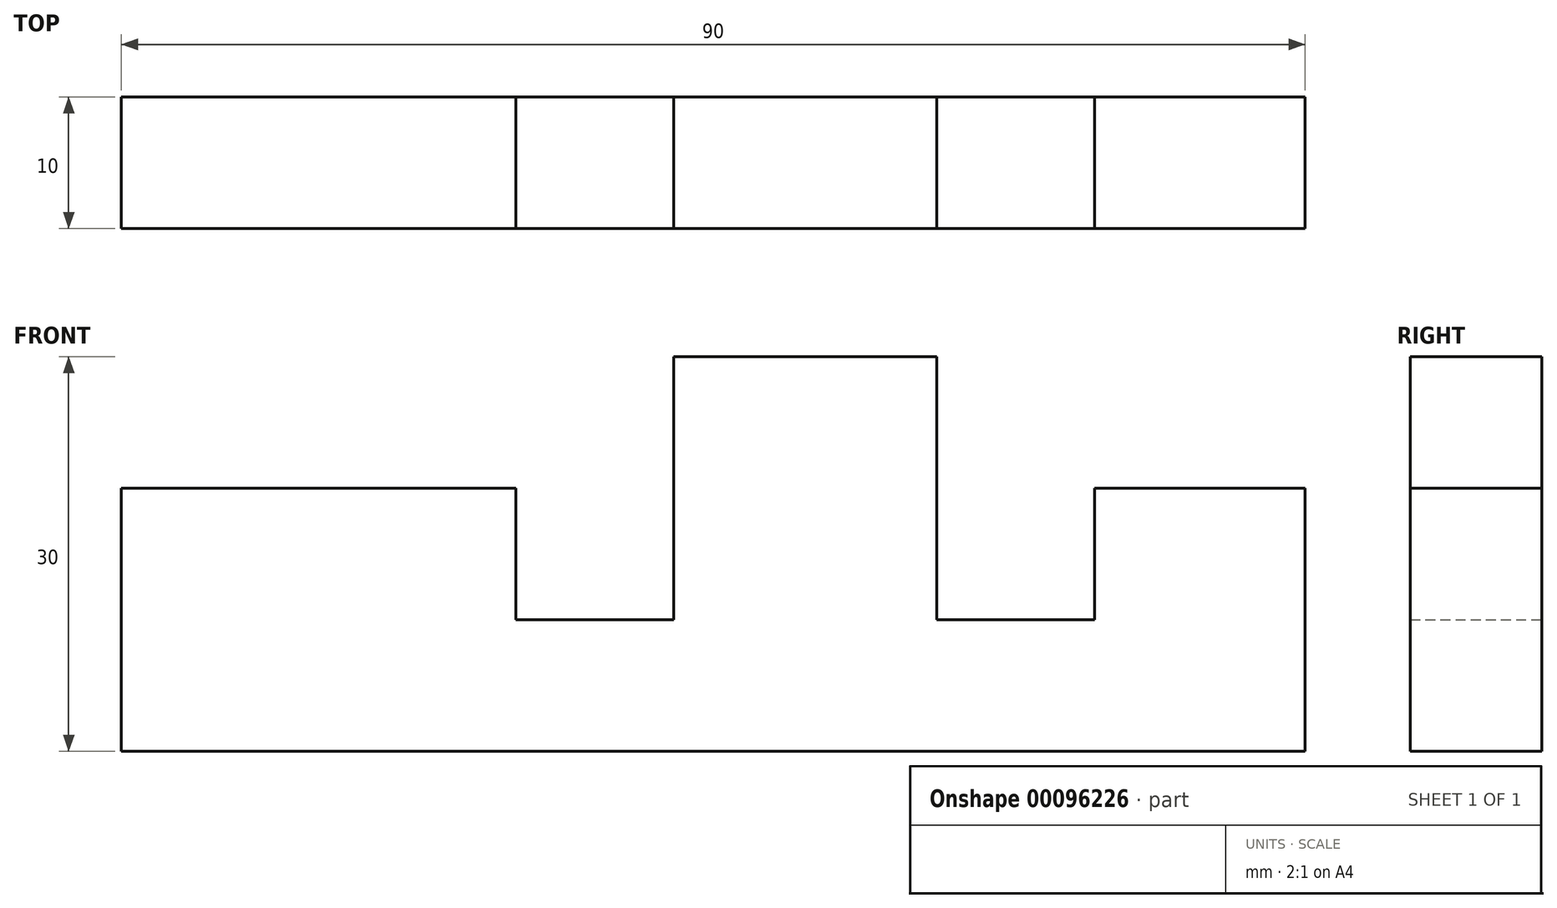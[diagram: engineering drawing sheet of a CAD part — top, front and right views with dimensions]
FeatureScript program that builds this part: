
annotation { "Feature Type Name" : "Feature", "Feature Type Description" : "" }
export const myFeature = defineFeature(function(context is Context, id is Id, definition is map)
    precondition{}
    {
        {
            var Q0;
            Q0=qCreatedBy(makeId("Front.planeOp"),FACE);
            var sketch = newSketch(context, id + "F0", { "sketchPlane" : qUnion([Q0])});
            skLineSegment(sketch, "E0", {"start": v(0, 0) * mm, "end": v(90, 0) * mm});
            skLineSegment(sketch, "E1", {"start": v(90, 0) * mm, "end": v(90, 20) * mm});
            skLineSegment(sketch, "E2", {"start": v(90, 20) * mm, "end": v(74, 20) * mm});
            skLineSegment(sketch, "E3", {"start": v(74, 20) * mm, "end": v(74, 10) * mm});
            skLineSegment(sketch, "E4", {"start": v(74, 10) * mm, "end": v(62, 10) * mm});
            skLineSegment(sketch, "E5", {"start": v(62, 10) * mm, "end": v(62, 30) * mm});
            skLineSegment(sketch, "E6", {"start": v(62, 30) * mm, "end": v(42, 30) * mm});
            skLineSegment(sketch, "E7", {"start": v(42, 30) * mm, "end": v(42, 10) * mm});
            skLineSegment(sketch, "E8", {"start": v(42, 10) * mm, "end": v(30, 10) * mm});
            skLineSegment(sketch, "E9", {"start": v(30, 10) * mm, "end": v(30, 20) * mm});
            skLineSegment(sketch, "E10", {"start": v(30, 20) * mm, "end": v(0, 20) * mm});
            skLineSegment(sketch, "E11", {"start": v(0, 20) * mm, "end": v(0, 0) * mm});
            skLineSegment(sketch, "E12", {"start": v(30, 20) * mm, "end": v(90, 20) * mm, "construction": true});
            skPoint(sketch, "E12.endSnap0", {"position": v(62, 20) * mm});
            skSolve(sketch);
        }
        {
            var Q0;
            Q0=makeQuery(id+"F0.imprint","IMPRINT",FACE,{"disambiguationData":[TD([[makeQuery(id+"F0.imprint","IMPRINT",EDGE,{"derivedFrom":sQuery(id+"F0.wireOp",EDGE,"E0")}),1.0]])]});
            extrude(context, id + "F1", {"entities" : qUnion([Q0]), "depth" : 10 * mm});
        }
    });
